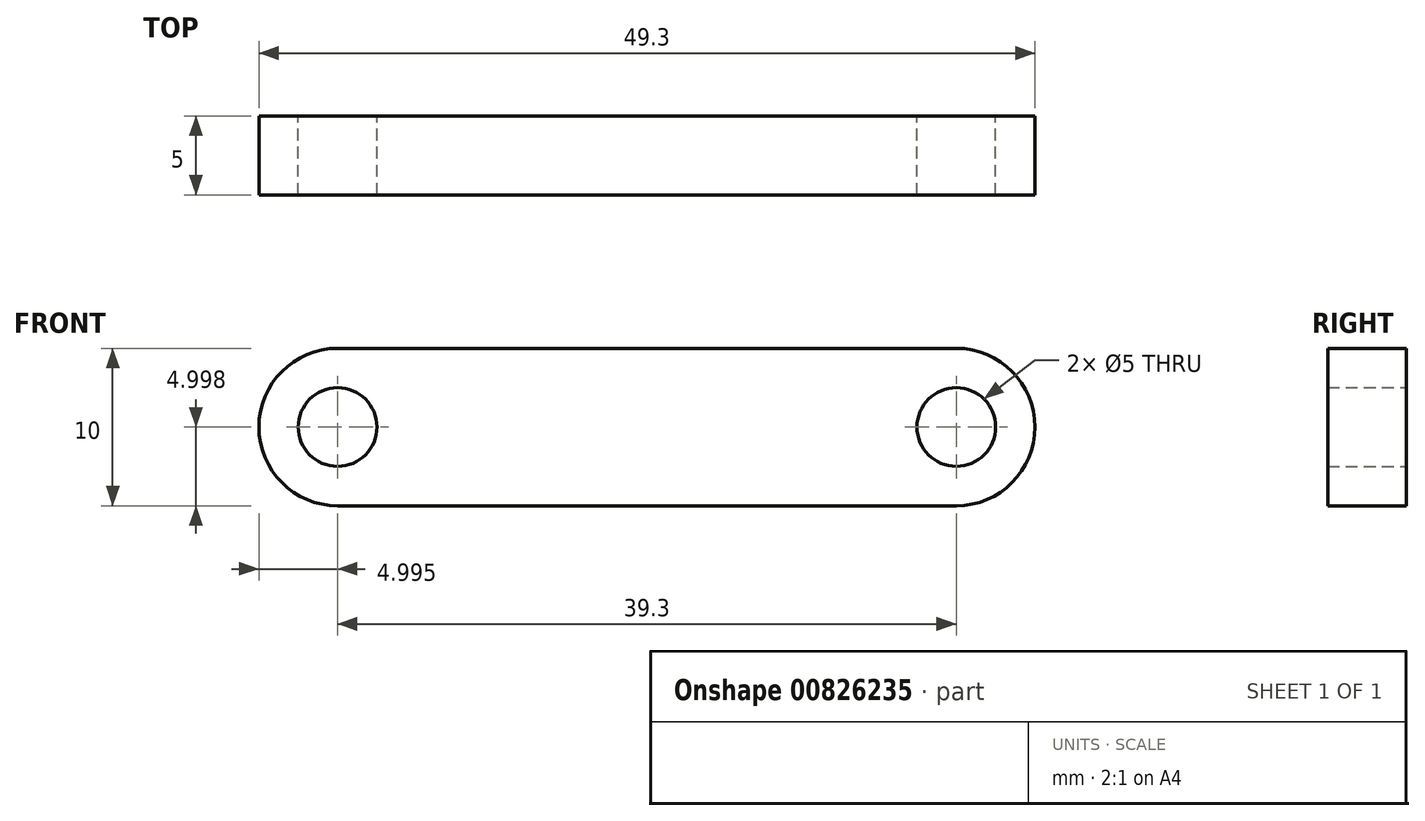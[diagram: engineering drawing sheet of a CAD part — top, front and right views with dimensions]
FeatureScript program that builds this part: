
annotation { "Feature Type Name" : "Feature", "Feature Type Description" : "" }
export const myFeature = defineFeature(function(context is Context, id is Id, definition is map)
    precondition{}
    {
        {
            var Q0;
            Q0=qCreatedBy(makeId("Front.planeOp"),FACE);
            var sketch = newSketch(context, id + "F0", { "sketchPlane" : qUnion([Q0])});
            skArc(sketch, "E0", {"start": v(-33.5, 14.77) * mm, "mid": v(-38.5, 9.77) * mm, "end": v(-33.5, 4.77) * mm});
            skArc(sketch, "E1", {"start": v(5.8, 4.77) * mm, "mid": v(10.8, 9.77) * mm, "end": v(5.8, 14.77) * mm});
            skLineSegment(sketch, "E2", {"start": v(-33.5, 14.77) * mm, "end": v(5.8, 14.77) * mm});
            skLineSegment(sketch, "E3", {"start": v(-33.5, 4.77) * mm, "end": v(5.8, 4.77) * mm});
            skCircle(sketch, "E4", {"center": v(-33.5, 9.77) * mm, "radius": 2.5 * mm});
            skCircle(sketch, "E5", {"center": v(5.8, 9.77) * mm, "radius": 2.5 * mm});
            skSolve(sketch);
        }
        {
            var Q0;
            Q0 = qSketchRegion(id + "F0", true);
            extrude(context, id + "F1", {"entities" : qUnion([Q0]), "depth" : 5 * mm, "offsetDistance" : 25 * mm});
        }
    });
